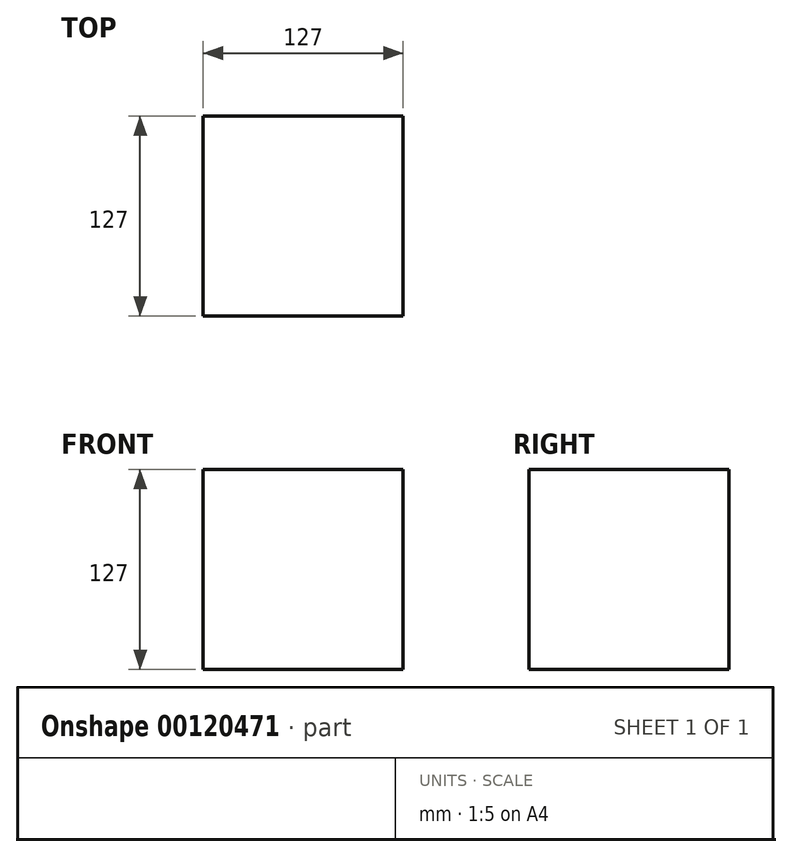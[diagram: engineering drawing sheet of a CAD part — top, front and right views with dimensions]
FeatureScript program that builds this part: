
annotation { "Feature Type Name" : "Feature", "Feature Type Description" : "" }
export const myFeature = defineFeature(function(context is Context, id is Id, definition is map)
    precondition{}
    {
        {
            var Q0;
            Q0=qCreatedBy(makeId("Front.planeOp"),FACE);
            var sketch = newSketch(context, id + "F0", { "sketchPlane" : qUnion([Q0])});
            skLineSegment(sketch, "E0.bottom", {"start": v(-63.5, 63.5) * mm, "end": v(63.5, 63.5) * mm});
            skLineSegment(sketch, "E0.top", {"start": v(-63.5, -63.5) * mm, "end": v(63.5, -63.5) * mm});
            skLineSegment(sketch, "E0.left", {"start": v(-63.5, 63.5) * mm, "end": v(-63.5, -63.5) * mm});
            skLineSegment(sketch, "E0.right", {"start": v(63.5, 63.5) * mm, "end": v(63.5, -63.5) * mm});
            skPoint(sketch, "E0.middle", {"position": v(0, 0) * mm});
            skSolve(sketch);
        }
        {
            var Q0;
            Q0 = qSketchRegion(id + "F0", true);
            extrude(context, id + "F1", {"entities" : qUnion([Q0]), "depth" : 127 * mm});
        }
    });
